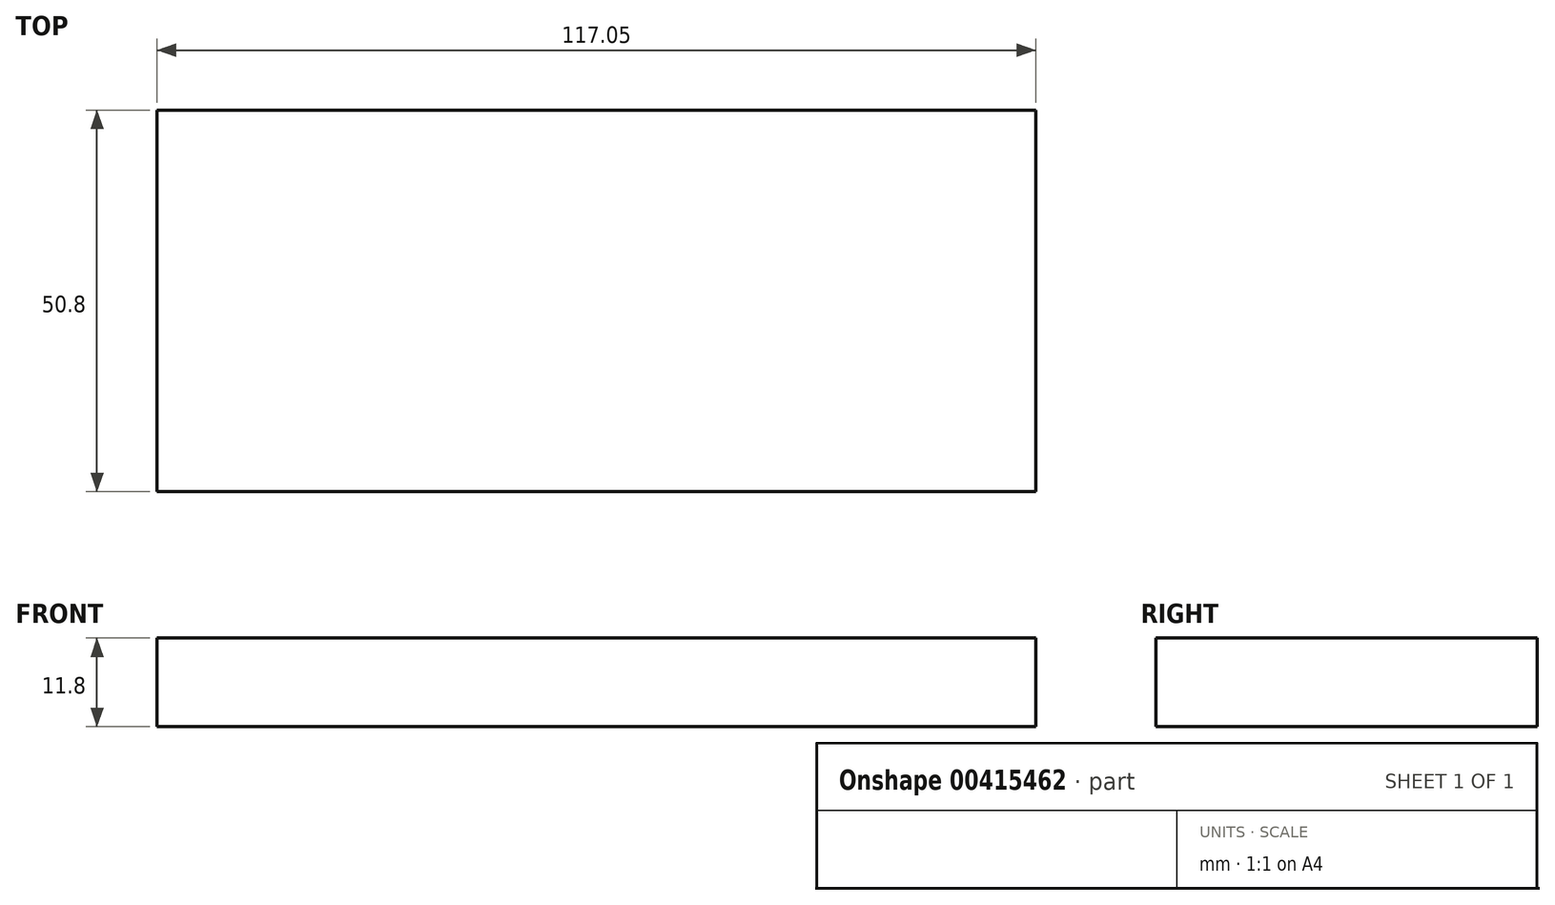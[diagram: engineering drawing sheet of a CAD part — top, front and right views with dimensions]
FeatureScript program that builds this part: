
annotation { "Feature Type Name" : "Feature", "Feature Type Description" : "" }
export const myFeature = defineFeature(function(context is Context, id is Id, definition is map)
    precondition{}
    {
        {
            var Q0;
            Q0=qCreatedBy(makeId("Front.planeOp"),FACE);
            var sketch = newSketch(context, id + "F0", { "sketchPlane" : qUnion([Q0])});
            skLineSegment(sketch, "E0.bottom", {"start": v(-58.15, 119.68) * mm, "end": v(58.9, 119.68) * mm});
            skLineSegment(sketch, "E0.top", {"start": v(-58.15, 131.48) * mm, "end": v(58.9, 131.48) * mm});
            skLineSegment(sketch, "E0.left", {"start": v(-58.15, 119.68) * mm, "end": v(-58.15, 131.48) * mm});
            skLineSegment(sketch, "E0.right", {"start": v(58.9, 119.68) * mm, "end": v(58.9, 131.48) * mm});
            skSolve(sketch);
        }
        {
            var Q0;
            Q0 = qSketchRegion(id + "F0", true);
            extrude(context, id + "F1", {"entities" : qUnion([Q0]), "depth" : 50.8 * mm});
        }
    });
